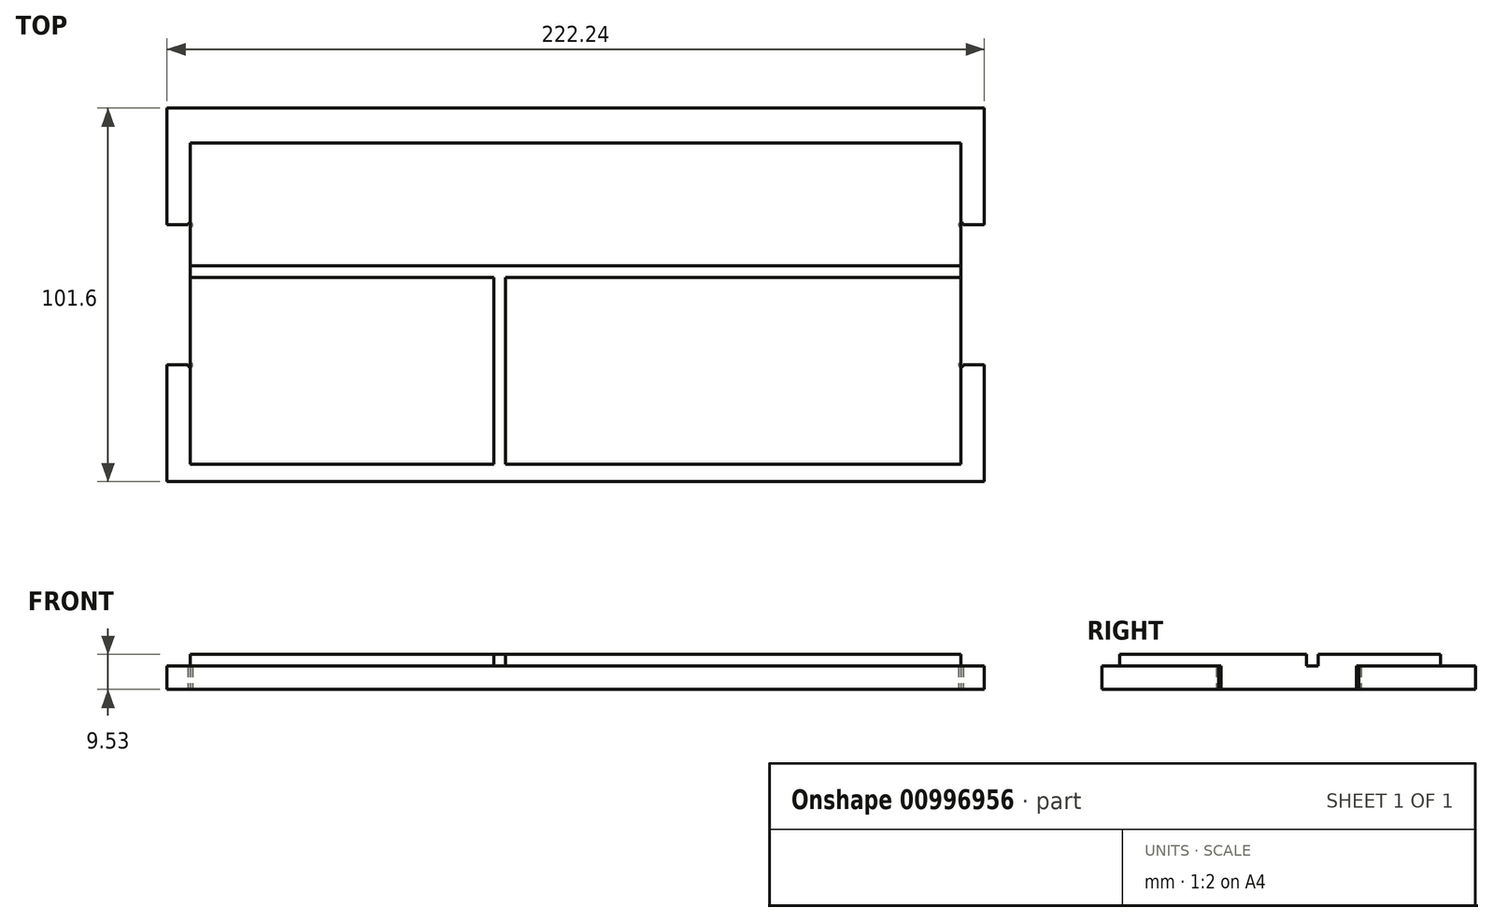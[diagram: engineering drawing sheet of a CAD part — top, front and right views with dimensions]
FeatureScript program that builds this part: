
annotation { "Feature Type Name" : "Feature", "Feature Type Description" : "" }
export const myFeature = defineFeature(function(context is Context, id is Id, definition is map)
    precondition{}
    {
        {
            var Q0;
            Q0=qCreatedBy(makeId("Top.planeOp"),FACE);
            var sketch = newSketch(context, id + "F0", { "sketchPlane" : qUnion([Q0])});
            skLineSegment(sketch, "E0.bottom", {"start": v(111.13, -50.8) * mm, "end": v(-111.12, -50.8) * mm});
            skLineSegment(sketch, "E0.top", {"start": v(111.12, 50.8) * mm, "end": v(-111.13, 50.8) * mm});
            skLineSegment(sketch, "E0.left", {"start": v(111.13, -50.8) * mm, "end": v(111.12, 50.8) * mm});
            skLineSegment(sketch, "E0.right", {"start": v(-111.12, -50.8) * mm, "end": v(-111.13, 50.8) * mm});
            skPoint(sketch, "E0.middle", {"position": v(0, 0) * mm});
            skSolve(sketch);
        }
        {
            var Q0;
            Q0=qSketchRegion(id+"F0",true);
            extrude(context, id + "F1", {"entities" : qUnion([Q0]), "depth" : 9.52 * mm, "offsetDistance" : 25.4 * mm});
        }
        {
            var Q0;
            Q0=makeQuery(id+"F1.opExtrude","CAP_FACE",FACE,{"disambiguationData":[OSD([sQuery(id+"F0.wireOp",EDGE,"E0.bottom"),sQuery(id+"F0.wireOp",EDGE,"E0.top"),sQuery(id+"F0.wireOp",EDGE,"E0.left"),sQuery(id+"F0.wireOp",EDGE,"E0.right")])],"isStart":false});
            var sketch = newSketch(context, id + "F2", { "sketchPlane" : qUnion([Q0])});
            skLineSegment(sketch, "E1.bottom", {"start": v(-111.13, 19.05) * mm, "end": v(-104.78, 19.05) * mm});
            skLineSegment(sketch, "E1.top", {"start": v(-111.13, -19.05) * mm, "end": v(-104.78, -19.05) * mm});
            skLineSegment(sketch, "E1.left", {"start": v(-111.13, 19.05) * mm, "end": v(-111.13, -19.05) * mm});
            skLineSegment(sketch, "E1.right", {"start": v(-104.78, 19.05) * mm, "end": v(-104.78, -19.05) * mm});
            skLineSegment(sketch, "E2.bottom", {"start": v(111.13, 19.05) * mm, "end": v(104.78, 19.05) * mm});
            skLineSegment(sketch, "E2.top", {"start": v(111.13, -19.05) * mm, "end": v(104.78, -19.05) * mm});
            skLineSegment(sketch, "E2.left", {"start": v(111.13, 19.05) * mm, "end": v(111.13, -19.05) * mm});
            skLineSegment(sketch, "E2.right", {"start": v(104.78, 19.05) * mm, "end": v(104.78, -19.05) * mm});
            skLineSegment(sketch, "E3", {"start": v(-111.13, 0) * mm, "end": v(111.12, 0) * mm, "construction": true});
            skSolve(sketch);
        }
        {
            var Q0;
            Q0=qSketchRegion(id+"F2",true);
            extrude(context, id + "F3", {"entities" : qUnion([Q0]), "operationType" : NewBodyOperationType.REMOVE, "endBound" : BoundingType.THROUGH_ALL, "oppositeDirection" : true, "depth" : 25.4 * mm, "offsetDistance" : 25.4 * mm});
        }
        {
            var Q0;
            Q0=makeQuery(id+"F1.opExtrude","CAP_FACE",FACE,{"disambiguationData":[OSD([sQuery(id+"F0.wireOp",EDGE,"E0.bottom"),sQuery(id+"F0.wireOp",EDGE,"E0.top"),sQuery(id+"F0.wireOp",EDGE,"E0.left"),sQuery(id+"F0.wireOp",EDGE,"E0.right")])],"isStart":false});
            var sketch = newSketch(context, id + "F4", { "sketchPlane" : qUnion([Q0])});
            skLineSegment(sketch, "E4", {"start": v(-104.78, 19.05) * mm, "end": v(-111.13, 19.05) * mm});
            skLineSegment(sketch, "E5", {"start": v(-111.13, 19.05) * mm, "end": v(-111.13, 50.8) * mm});
            skLineSegment(sketch, "E6", {"start": v(-111.13, 50.8) * mm, "end": v(111.12, 50.8) * mm});
            skLineSegment(sketch, "E7", {"start": v(111.12, 50.8) * mm, "end": v(111.12, 19.05) * mm});
            skLineSegment(sketch, "E8", {"start": v(111.12, 19.05) * mm, "end": v(104.78, 19.05) * mm});
            skLineSegment(sketch, "E9", {"start": v(104.78, 19.05) * mm, "end": v(104.78, 41.28) * mm});
            skLineSegment(sketch, "E10", {"start": v(104.78, 41.28) * mm, "end": v(-104.78, 41.28) * mm});
            skLineSegment(sketch, "E11", {"start": v(-104.78, 41.28) * mm, "end": v(-104.78, 19.05) * mm});
            skLineSegment(sketch, "E12", {"start": v(111.13, -19.05) * mm, "end": v(111.13, -50.8) * mm});
            skLineSegment(sketch, "E13", {"start": v(111.13, -50.8) * mm, "end": v(-111.12, -50.8) * mm});
            skLineSegment(sketch, "E14", {"start": v(-111.12, -50.8) * mm, "end": v(-111.12, -19.05) * mm});
            skLineSegment(sketch, "E15", {"start": v(-111.12, -19.05) * mm, "end": v(-104.78, -19.05) * mm});
            skLineSegment(sketch, "E16", {"start": v(-104.77, -19.05) * mm, "end": v(-104.77, -46.04) * mm});
            skLineSegment(sketch, "E17", {"start": v(-104.77, -46.04) * mm, "end": v(104.78, -46.04) * mm});
            skLineSegment(sketch, "E18", {"start": v(104.78, -46.04) * mm, "end": v(104.78, -19.05) * mm});
            skLineSegment(sketch, "E19", {"start": v(104.78, -19.05) * mm, "end": v(111.13, -19.05) * mm});
            skSolve(sketch);
        }
        {
            var Q0;
            Q0=makeQuery(id+"F4.imprint","IMPRINT",FACE,{"disambiguationData":[TD([[makeQuery(id+"F4.imprint","IMPRINT",EDGE,{"derivedFrom":sQuery(id+"F4.wireOp",EDGE,"E12")}),1.0]])]});
            var Q1;
            Q1=makeQuery(id+"F4.imprint","IMPRINT",FACE,{"disambiguationData":[TD([[makeQuery(id+"F4.imprint","IMPRINT",EDGE,{"derivedFrom":sQuery(id+"F4.wireOp",EDGE,"E4")}),1.0]])]});
            extrude(context, id + "F5", {"entities" : qUnion([Q0, Q1]), "operationType" : NewBodyOperationType.REMOVE, "oppositeDirection" : true, "depth" : 3.17 * mm, "offsetDistance" : 25.4 * mm});
        }
        {
            var Q0;
            Q0=makeQuery(id+"F1.opExtrude","CAP_FACE",FACE,{"disambiguationData":[OSD([sQuery(id+"F0.wireOp",EDGE,"E0.bottom"),sQuery(id+"F0.wireOp",EDGE,"E0.top"),sQuery(id+"F0.wireOp",EDGE,"E0.left"),sQuery(id+"F0.wireOp",EDGE,"E0.right")])],"isStart":false});
            var sketch = newSketch(context, id + "F6", { "sketchPlane" : qUnion([Q0])});
            skLineSegment(sketch, "E20.bottom", {"start": v(-104.78, 7.94) * mm, "end": v(104.78, 7.94) * mm});
            skLineSegment(sketch, "E20.top", {"start": v(-104.78, 4.76) * mm, "end": v(104.78, 4.76) * mm});
            skLineSegment(sketch, "E20.left", {"start": v(-104.78, 7.94) * mm, "end": v(-104.78, 4.76) * mm});
            skLineSegment(sketch, "E20.right", {"start": v(104.78, 7.94) * mm, "end": v(104.78, 4.76) * mm});
            skLineSegment(sketch, "E21", {"start": v(-19.05, 4.76) * mm, "end": v(-19.05, -46.04) * mm});
            skLineSegment(sketch, "E22", {"start": v(-22.23, -46.04) * mm, "end": v(-19.05, -46.04) * mm});
            skLineSegment(sketch, "E23", {"start": v(-22.23, -46.04) * mm, "end": v(-22.23, 4.76) * mm});
            skSolve(sketch);
        }
        {
            var Q0;
            Q0=qSketchRegion(id+"F6",true);
            extrude(context, id + "F7", {"entities" : qUnion([Q0]), "operationType" : NewBodyOperationType.REMOVE, "oppositeDirection" : true, "depth" : 3.17 * mm, "offsetDistance" : 25.4 * mm});
        }
        {
            var Q0;
            Q0=makeQuery(id+"F1.opExtrude","CAP_FACE",FACE,{"disambiguationData":[OSD([sQuery(id+"F0.wireOp",EDGE,"E0.bottom"),sQuery(id+"F0.wireOp",EDGE,"E0.top"),sQuery(id+"F0.wireOp",EDGE,"E0.left"),sQuery(id+"F0.wireOp",EDGE,"E0.right")])],"isStart":true});
            var sketch = newSketch(context, id + "F8", { "sketchPlane" : qUnion([Q0])});
            skArc(sketch, "E24", {"start": v(104.78, 18.42) * mm, "mid": v(104.33, 19.5) * mm, "end": v(105.4, 19.05) * mm});
            skArc(sketch, "E25", {"start": v(105.4, -19.05) * mm, "mid": v(104.33, -19.5) * mm, "end": v(104.78, -18.41) * mm});
            skArc(sketch, "E26", {"start": v(-105.4, -19.05) * mm, "mid": v(-104.33, -19.5) * mm, "end": v(-104.78, -18.41) * mm});
            skArc(sketch, "E27", {"start": v(-104.78, 18.41) * mm, "mid": v(-104.33, 19.5) * mm, "end": v(-105.4, 19.05) * mm});
            skLineSegment(sketch, "E28", {"start": v(-104.78, -19.05) * mm, "end": v(-104.78, -18.41) * mm});
            skLineSegment(sketch, "E29", {"start": v(-104.78, -19.05) * mm, "end": v(-105.4, -19.05) * mm});
            skLineSegment(sketch, "E30", {"start": v(-104.78, 19.05) * mm, "end": v(-105.4, 19.05) * mm});
            skLineSegment(sketch, "E31", {"start": v(-104.78, 19.05) * mm, "end": v(-104.78, 18.41) * mm});
            skLineSegment(sketch, "E32", {"start": v(104.78, -19.05) * mm, "end": v(104.78, -18.41) * mm});
            skLineSegment(sketch, "E33", {"start": v(104.78, -19.05) * mm, "end": v(105.4, -19.05) * mm});
            skLineSegment(sketch, "E34", {"start": v(104.78, 19.05) * mm, "end": v(104.78, 18.42) * mm});
            skLineSegment(sketch, "E35", {"start": v(104.78, 19.05) * mm, "end": v(105.4, 19.05) * mm});
            skSolve(sketch);
        }
        {
            var Q0;
            Q0=qSketchRegion(id+"F8",true);
            var Q1;
            Q1=makeQuery(id+"F5.boolean.opBoolean","COPY",FACE,{"derivedFrom":makeQuery(id+"F5.opExtrude","CAP_FACE",FACE,{"disambiguationData":[OSD([sQuery(id+"F4.wireOp",EDGE,"E4"),sQuery(id+"F4.wireOp",EDGE,"E5"),sQuery(id+"F4.wireOp",EDGE,"E6"),sQuery(id+"F4.wireOp",EDGE,"E7"),sQuery(id+"F4.wireOp",EDGE,"E8"),sQuery(id+"F4.wireOp",EDGE,"E9"),sQuery(id+"F4.wireOp",EDGE,"E10"),sQuery(id+"F4.wireOp",EDGE,"E11")])],"isStart":false})});
            extrude(context, id + "F9", {"entities" : qUnion([Q0]), "operationType" : NewBodyOperationType.REMOVE, "endBound" : BoundingType.UP_TO_SURFACE, "oppositeDirection" : true, "depth" : 25.4 * mm, "endBoundEntityFace" : qUnion([Q1]), "offsetDistance" : 25.4 * mm});
        }
    });
